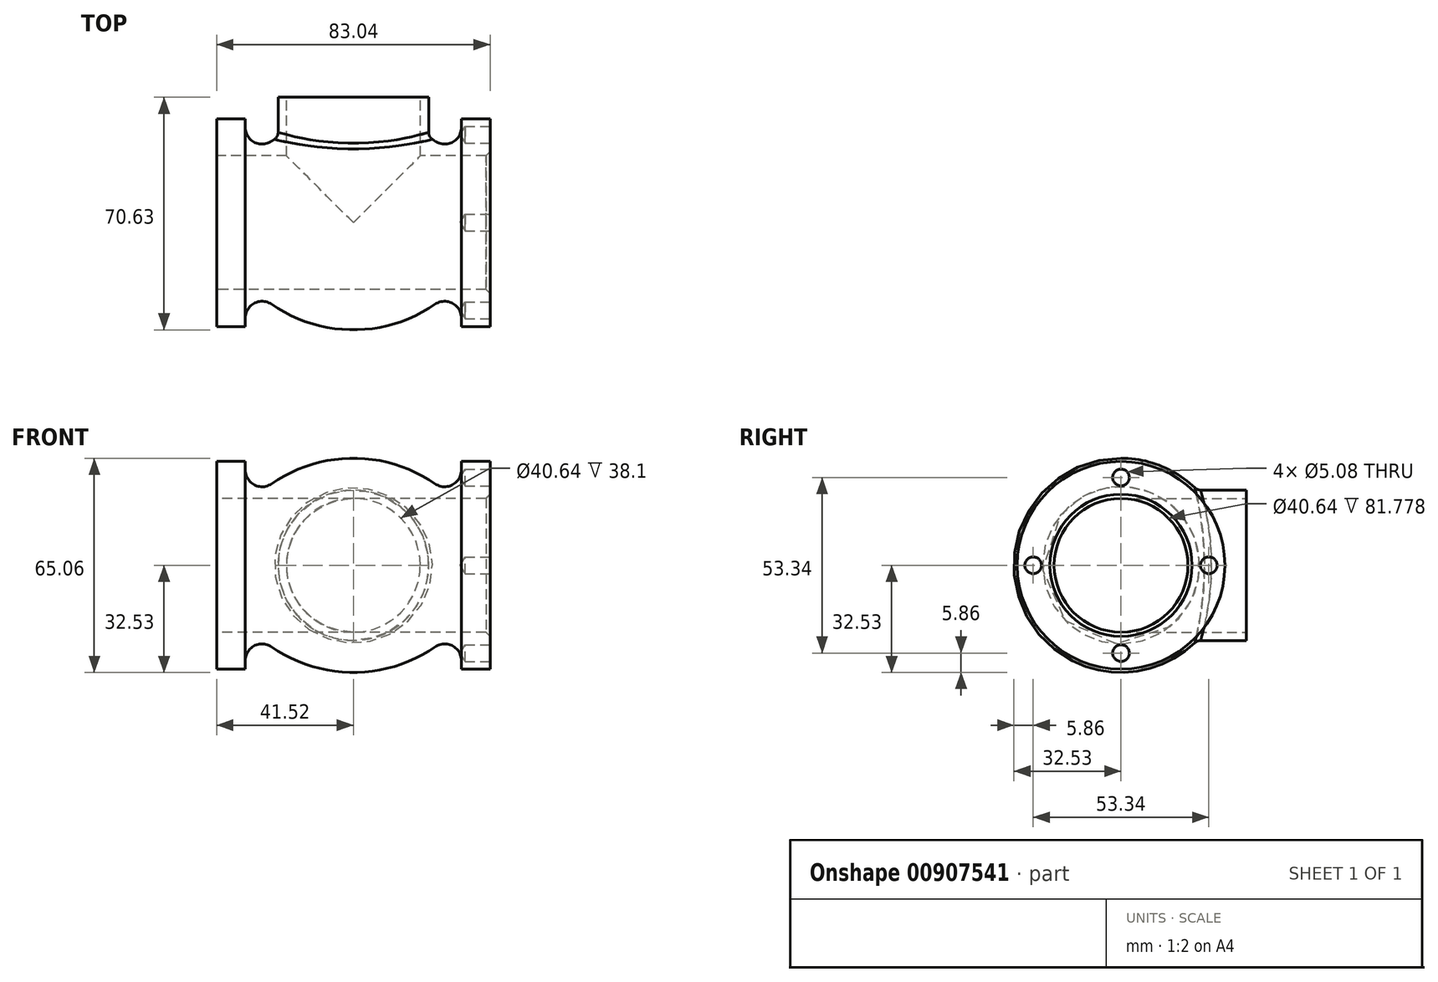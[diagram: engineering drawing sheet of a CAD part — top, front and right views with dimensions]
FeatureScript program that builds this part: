
annotation { "Feature Type Name" : "Feature", "Feature Type Description" : "" }
export const myFeature = defineFeature(function(context is Context, id is Id, definition is map)
    precondition{}
    {
        {
            var Q0;
            Q0=qCreatedBy(makeId("Front.planeOp"),FACE);
            var sketch = newSketch(context, id + "F0", { "sketchPlane" : qUnion([Q0])});
            skLineSegment(sketch, "E0.top", {"start": v(-41.52, 31.54) * mm, "end": v(-32.82, 31.54) * mm});
            skLineSegment(sketch, "E0.left", {"start": v(-41.52, 0) * mm, "end": v(-41.52, 31.54) * mm});
            skLineSegment(sketch, "E0.right", {"start": v(-32.82, 17.65) * mm, "end": v(-32.82, 31.54) * mm});
            skArc(sketch, "E1", {"start": v(0, 32.53) * mm, "mid": v(-18.01, 28.63) * mm, "end": v(-32.82, 17.65) * mm});
            skLineSegment(sketch, "E2", {"start": v(0, 32.53) * mm, "end": v(0, 0) * mm});
            skLineSegment(sketch, "E3", {"start": v(0, 0) * mm, "end": v(-41.52, 0) * mm});
            skSolve(sketch);
        }
        {
            var Q0;
            Q0=makeQuery(id+"F0.imprint","IMPRINT",FACE,{"disambiguationData":[TD([[makeQuery(id+"F0.imprint","IMPRINT",EDGE,{"derivedFrom":sQuery(id+"F0.wireOp",EDGE,"E0.top")}),-1.0]])]});
            var Q1;
            Q1=sQuery(id+"F0.wireOp",EDGE,"E3");
            revolve(context, id + "F1", {"surfaceOperationType" : NewSurfaceOperationType.NEW, "entities" : qUnion([Q0]), "axis" : qUnion([Q1]), "revolveType" : RevolveType.FULL});
        }
        {
            var Q0;
            Q0=makeQuery(id+"F1.opRevolve","SWEPT_BODY",BODY,{"disambiguationData":[OSD([sQuery(id+"F0.wireOp",EDGE,"E0.top"),sQuery(id+"F0.wireOp",EDGE,"E0.left"),sQuery(id+"F0.wireOp",EDGE,"E0.right"),sQuery(id+"F0.wireOp",EDGE,"E1"),sQuery(id+"F0.wireOp",EDGE,"E2"),sQuery(id+"F0.wireOp",EDGE,"E3")])]});
            var Q1;
            Q1=qCreatedBy(makeId("Right.planeOp"),FACE);
            mirror(context, id + "F2", {"operationType" : NewBodyOperationType.ADD, "entities" : qUnion([Q0]), "mirrorPlane" : qUnion([Q1])});
        }
        {
            var Q0;
            Q0=makeQuery(id+"F2.opPattern","COPY",EDGE,{"derivedFrom":makeQuery(id+"F1.opRevolve","SWEPT_EDGE",EDGE,{"disambiguationData":[OSD([sQuery(id+"F0.wireOp",EDGE,"E0.right"),sQuery(id+"F0.wireOp",EDGE,"E1")])]}),"instanceName":"1"});
            var Q1;
            Q1=makeQuery(id+"F1.opRevolve","SWEPT_EDGE",EDGE,{"disambiguationData":[OSD([sQuery(id+"F0.wireOp",EDGE,"E0.right"),sQuery(id+"F0.wireOp",EDGE,"E1")])]});
            fillet(context, id + "F3", {"entities" : qUnion([Q0, Q1]), "radius" : 5.08 * mm, "tangentPropagation" : true, "allowEdgeOverflow" : false});
        }
        {
            var Q0;
            Q0=makeQuery(id+"F1.opRevolve","SWEPT_FACE",FACE,{"disambiguationData":[OSD([sQuery(id+"F0.wireOp",EDGE,"E0.left")])]});
            var sketch = newSketch(context, id + "F4", { "sketchPlane" : qUnion([Q0])});
            skCircle(sketch, "E4", {"center": v(0, 0) * mm, "radius": 20.32 * mm});
            skSolve(sketch);
        }
        {
            var Q0;
            Q0=qCreatedBy(makeId("Front.planeOp"),FACE);
            var sketch = newSketch(context, id + "F5", { "sketchPlane" : qUnion([Q0])});
            skCircle(sketch, "E5", {"center": v(0, 0) * mm, "radius": 22.86 * mm});
            skSolve(sketch);
        }
        {
            var Q0;
            Q0 = qSketchRegion(id + "F5", true);
            extrude(context, id + "F6", {"entities" : qUnion([Q0]), "operationType" : NewBodyOperationType.ADD, "oppositeDirection" : true, "depth" : 38.1 * mm, "offsetDistance" : 25.4 * mm});
        }
        {
            var Q0;
            {var subQ0=makeQuery(id+"F1.opRevolve","SWEPT_FACE",FACE,{"disambiguationData":[OSD([sQuery(id+"F0.wireOp",EDGE,"E1")])]});Q0=makeQuery(id+"F6.boolean.opBoolean","INTERSECT",EDGE,{"derivedFrom":[makeQuery(id+"F2.boolean.opBoolean","MERGE",FACE,{"derivedFrom":[subQ0,makeQuery(id+"F2.opPattern","COPY",FACE,{"derivedFrom":subQ0,"instanceName":"1"})]}),makeQuery(id+"F6.opExtrude","SWEPT_FACE",FACE,{"disambiguationData":[OSD([sQuery(id+"F5.wireOp",EDGE,"E5")])]})]});}
            fillet(context, id + "F7", {"entities" : qUnion([Q0]), "radius" : 2.54 * mm, "tangentPropagation" : true, "allowEdgeOverflow" : false});
        }
        {
            var Q0;
            Q0=makeQuery(id+"F4.imprint","IMPRINT",FACE,{"disambiguationData":[TD([[makeQuery(id+"F4.imprint","IMPRINT",EDGE,{"derivedFrom":sQuery(id+"F4.wireOp",EDGE,"E4")}),1.0]])]});
            extrude(context, id + "F8", {"entities" : qUnion([Q0]), "operationType" : NewBodyOperationType.REMOVE, "endBound" : BoundingType.THROUGH_ALL, "oppositeDirection" : true, "depth" : 25.4 * mm, "offsetDistance" : 25.4 * mm});
        }
        {
            var Q0;
            Q0=makeQuery(id+"F6.opExtrude","CAP_FACE",FACE,{"disambiguationData":[OSD([sQuery(id+"F5.wireOp",EDGE,"E5")])],"isStart":false});
            var sketch = newSketch(context, id + "F9", { "sketchPlane" : qUnion([Q0])});
            skCircle(sketch, "E6", {"center": v(0, 0) * mm, "radius": 20.32 * mm});
            skSolve(sketch);
        }
        {
            var Q0;
            Q0=makeQuery(id+"F9.imprint","IMPRINT",FACE,{"disambiguationData":[TD([[makeQuery(id+"F9.imprint","IMPRINT",EDGE,{"derivedFrom":sQuery(id+"F9.wireOp",EDGE,"E6")}),1.0]])]});
            extrude(context, id + "F10", {"entities" : qUnion([Q0]), "operationType" : NewBodyOperationType.REMOVE, "endBound" : BoundingType.UP_TO_NEXT, "oppositeDirection" : true, "depth" : 25.4 * mm, "offsetDistance" : 25.4 * mm});
        }
        {
            var Q0;
            Q0=makeQuery(id+"F10.boolean.opBoolean","COPY",EDGE,{"derivedFrom":makeQuery(id+"F10.opExtrude","CAP_EDGE",EDGE,{"disambiguationData":[OSD([sQuery(id+"F9.wireOp",EDGE,"E6")])],"isStart":true})});
            var Q1;
            Q1=makeQuery(id+"F8.boolean.opBoolean","COPY",EDGE,{"derivedFrom":makeQuery(id+"F8.opExtrude","CAP_EDGE",EDGE,{"disambiguationData":[OSD([sQuery(id+"F4.wireOp",EDGE,"E4")])],"isStart":true})});
            var Q2;
            Q2=makeQuery(id+"F8.boolean.opBoolean","INTERSECT",EDGE,{"derivedFrom":[makeQuery(id+"F2.opPattern","COPY",FACE,{"derivedFrom":makeQuery(id+"F1.opRevolve","SWEPT_FACE",FACE,{"disambiguationData":[OSD([sQuery(id+"F0.wireOp",EDGE,"E0.left")])]}),"instanceName":"1"}),makeQuery(id+"F8.opExtrude","SWEPT_FACE",FACE,{"disambiguationData":[OSD([sQuery(id+"F4.wireOp",EDGE,"E4")])]})]});
            chamfer(context, id + "F11", {"entities" : qUnion([Q0, Q1, Q2]), "width" : 1.27 * mm, "tangentPropagation" : true});
        }
        {
            var Q0;
            Q0=makeQuery(id+"F2.opPattern","COPY",FACE,{"derivedFrom":makeQuery(id+"F1.opRevolve","SWEPT_FACE",FACE,{"disambiguationData":[OSD([sQuery(id+"F0.wireOp",EDGE,"E0.left")])]}),"instanceName":"1"});
            var sketch = newSketch(context, id + "F12", { "sketchPlane" : qUnion([Q0])});
            skPoint(sketch, "E7", {"position": v(-26.67, 0) * mm});
            skPoint(sketch, "E8", {"position": v(0, 26.67) * mm});
            skPoint(sketch, "E9", {"position": v(26.67, 0) * mm});
            skPoint(sketch, "E10", {"position": v(0, -26.67) * mm});
            skCircle(sketch, "E11", {"center": v(0, 0) * mm, "radius": 26.67 * mm});
            skSolve(sketch);
        }
        {
            var Q0;
            Q0=sQuery(id+"F12.wireOp",VERTEX,"E8");
            var Q1;
            Q1=sQuery(id+"F12.wireOp",VERTEX,"E7");
            var Q2;
            Q2=sQuery(id+"F12.wireOp",VERTEX,"E10");
            var Q3;
            Q3=sQuery(id+"F12.wireOp",VERTEX,"E9");
            var Q4;
            Q4=makeQuery(id+"F1.opRevolve","SWEPT_BODY",BODY,{"disambiguationData":[OSD([sQuery(id+"F0.wireOp",EDGE,"E0.top"),sQuery(id+"F0.wireOp",EDGE,"E0.left"),sQuery(id+"F0.wireOp",EDGE,"E0.right"),sQuery(id+"F0.wireOp",EDGE,"E1"),sQuery(id+"F0.wireOp",EDGE,"E2"),sQuery(id+"F0.wireOp",EDGE,"E3")])]});
            hole(context, id + "F13", {"style" : HoleStyle.SIMPLE, "endStyle" : HoleEndStyle.BLIND, "holeDiameter" : 5.08 * mm, "majorDiameter" : 6.35 * mm, "holeDepth" : 7.62 * mm, "isTappedThrough" : true, "tappedDepth" : 12.7 * mm, "tapClearance" : 3, "locations" : qUnion([Q0, Q1, Q2, Q3]), "scope" : qUnion([Q4])});
        }
    });
